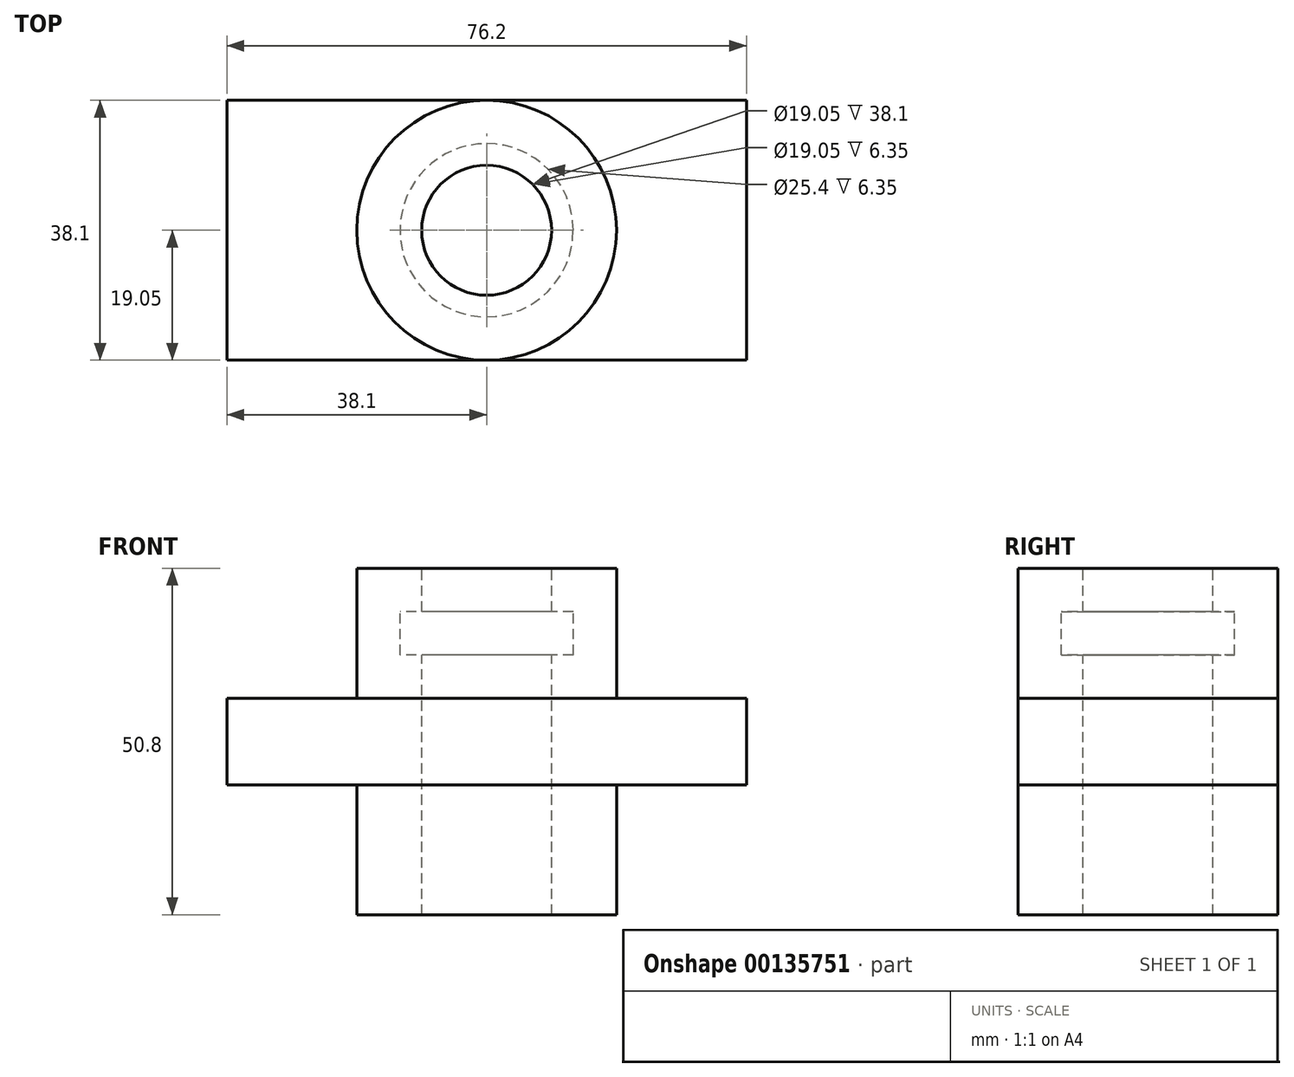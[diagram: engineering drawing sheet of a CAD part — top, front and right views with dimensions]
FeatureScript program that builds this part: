
annotation { "Feature Type Name" : "Feature", "Feature Type Description" : "" }
export const myFeature = defineFeature(function(context is Context, id is Id, definition is map)
    precondition{}
    {
        {
            var Q0;
            Q0=qCreatedBy(makeId("Top.planeOp"),FACE);
            var sketch = newSketch(context, id + "F0", { "sketchPlane" : qUnion([Q0])});
            skLineSegment(sketch, "E0", {"start": v(0, 0) * mm, "end": v(0, 38.1) * mm});
            skLineSegment(sketch, "E1", {"start": v(0, 38.1) * mm, "end": v(76.2, 38.1) * mm});
            skLineSegment(sketch, "E2", {"start": v(76.2, 38.1) * mm, "end": v(76.2, 0) * mm});
            skLineSegment(sketch, "E3", {"start": v(76.2, 0) * mm, "end": v(0, 0) * mm});
            skSolve(sketch);
        }
        {
            var Q0;
            Q0 = qSketchRegion(id + "F0", true);
            extrude(context, id + "F1", {"entities" : qUnion([Q0]), "depth" : 12.7 * mm});
        }
        {
            var Q0;
            Q0=makeQuery(id+"F1.opExtrude","CAP_FACE",FACE,{"disambiguationData":[OSD([sQuery(id+"F0.wireOp",EDGE,"E0"),sQuery(id+"F0.wireOp",EDGE,"E1"),sQuery(id+"F0.wireOp",EDGE,"E2"),sQuery(id+"F0.wireOp",EDGE,"E3")])],"isStart":false});
            var sketch = newSketch(context, id + "F2", { "sketchPlane" : qUnion([Q0])});
            skCircle(sketch, "E4", {"center": v(38.1, 19.05) * mm, "radius": 19.05 * mm});
            skPoint(sketch, "E4.centerSnap0", {"position": v(76.2, 19.05) * mm});
            skSolve(sketch);
        }
        {
            var Q0;
            Q0 = qSketchRegion(id + "F2", true);
            extrude(context, id + "F3", {"entities" : qUnion([Q0]), "operationType" : NewBodyOperationType.ADD, "depth" : 19.05 * mm});
        }
        {
            var Q0;
            Q0=makeQuery(id+"F1.opExtrude","CAP_FACE",FACE,{"disambiguationData":[OSD([sQuery(id+"F0.wireOp",EDGE,"E0"),sQuery(id+"F0.wireOp",EDGE,"E1"),sQuery(id+"F0.wireOp",EDGE,"E2"),sQuery(id+"F0.wireOp",EDGE,"E3")])],"isStart":true});
            var sketch = newSketch(context, id + "F4", { "sketchPlane" : qUnion([Q0])});
            skCircle(sketch, "E5", {"center": v(38.1, -19.05) * mm, "radius": 19.05 * mm});
            skSolve(sketch);
        }
        {
            var Q0;
            Q0 = qSketchRegion(id + "F4", true);
            extrude(context, id + "F5", {"entities" : qUnion([Q0]), "operationType" : NewBodyOperationType.ADD, "depth" : 19.05 * mm});
        }
        {
            var Q0;
            Q0=makeQuery(id+"F3.opExtrude","CAP_FACE",FACE,{"disambiguationData":[OSD([sQuery(id+"F2.wireOp",EDGE,"E4")])],"isStart":false});
            var sketch = newSketch(context, id + "F6", { "sketchPlane" : qUnion([Q0])});
            skCircle(sketch, "E6", {"center": v(38.1, 19.05) * mm, "radius": 9.53 * mm});
            skSolve(sketch);
        }
        {
            var Q0;
            Q0=makeQuery(id+"F3.opExtrude","CAP_FACE",FACE,{"disambiguationData":[OSD([sQuery(id+"F2.wireOp",EDGE,"E4")])],"isStart":false});
            var sketch = newSketch(context, id + "F7", { "sketchPlane" : qUnion([Q0])});
            skCircle(sketch, "E7", {"center": v(38.1, 19.05) * mm, "radius": 12.7 * mm});
            skSolve(sketch);
        }
        {
            var Q0;
            Q0 = qSketchRegion(id + "F7", true);
            extrude(context, id + "F8", {"entities" : qUnion([Q0]), "operationType" : NewBodyOperationType.REMOVE, "oppositeDirection" : true, "depth" : 12.7 * mm});
        }
        {
            var Q0;
            Q0=makeQuery(id+"F3.opExtrude","CAP_FACE",FACE,{"disambiguationData":[OSD([sQuery(id+"F2.wireOp",EDGE,"E4")])],"isStart":false});
            var sketch = newSketch(context, id + "F9", { "sketchPlane" : qUnion([Q0])});
            skCircle(sketch, "E8", {"center": v(38.1, 19.05) * mm, "radius": 19.05 * mm});
            skSolve(sketch);
        }
        {
            var Q0;
            Q0 = qSketchRegion(id + "F9", true);
            extrude(context, id + "F10", {"entities" : qUnion([Q0]), "operationType" : NewBodyOperationType.ADD, "oppositeDirection" : true, "depth" : 6.35 * mm});
        }
        {
            var Q0;
            Q0 = qSketchRegion(id + "F6", true);
            extrude(context, id + "F11", {"entities" : qUnion([Q0]), "operationType" : NewBodyOperationType.REMOVE, "endBound" : BoundingType.THROUGH_ALL, "oppositeDirection" : true, "depth" : 25.4 * mm});
        }
    });
